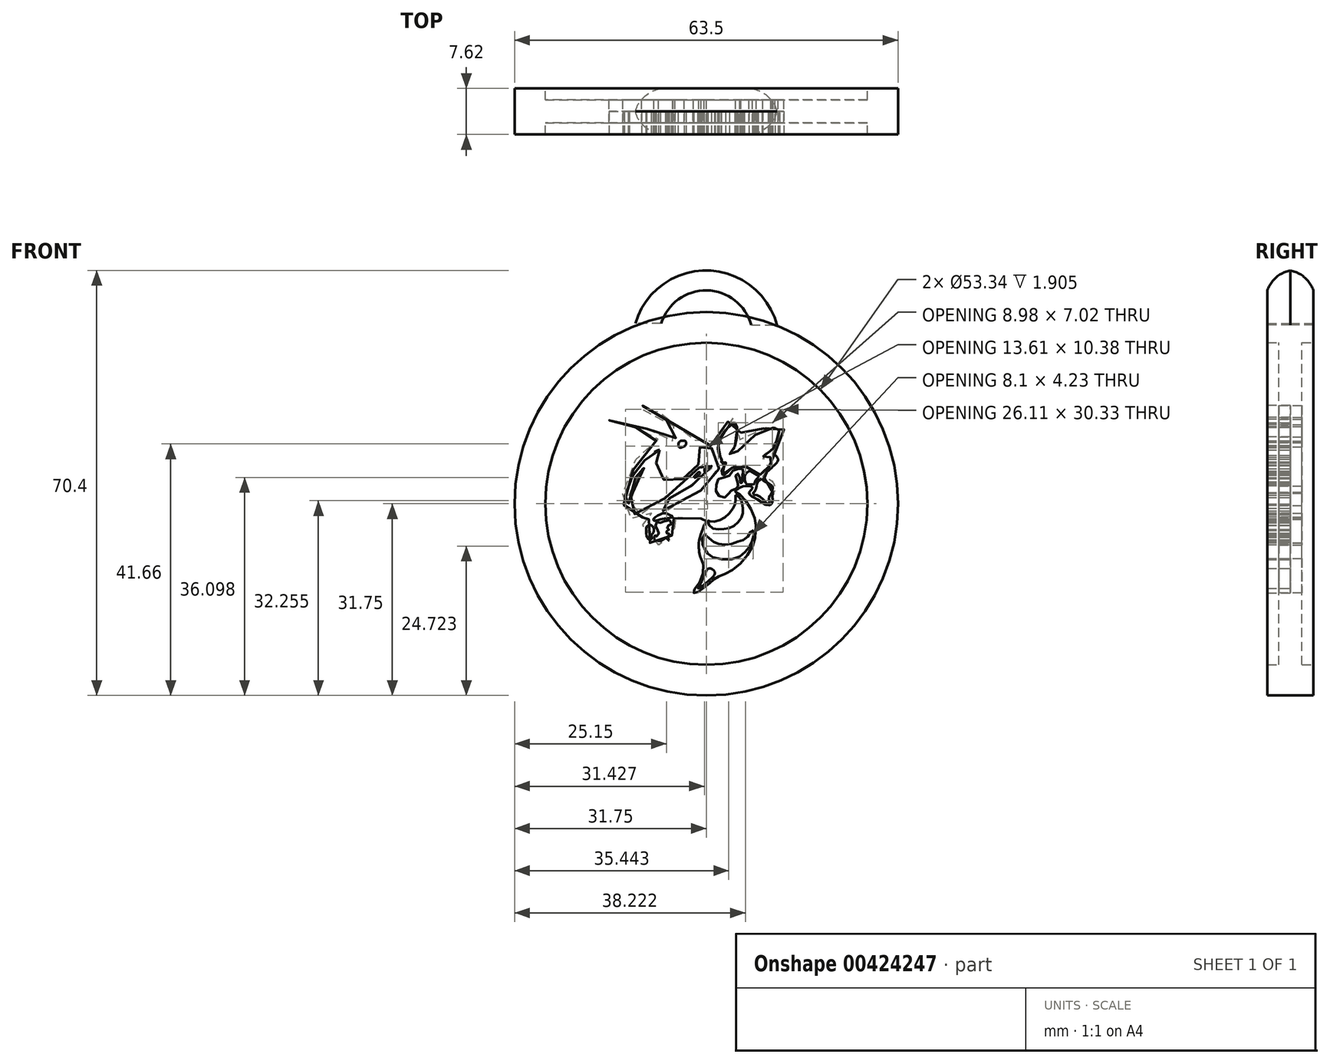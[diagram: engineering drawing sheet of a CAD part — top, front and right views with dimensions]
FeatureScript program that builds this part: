
annotation { "Feature Type Name" : "Feature", "Feature Type Description" : "" }
export const myFeature = defineFeature(function(context is Context, id is Id, definition is map)
    precondition{}
    {
        {
            var Q0;
            Q0=qCreatedBy(makeId("Front.planeOp"),FACE);
            var sketch = newSketch(context, id + "F0", { "sketchPlane" : qUnion([Q0])});
            skCircle(sketch, "E0", {"center": v(0, 0) * mm, "radius": 31.75 * mm});
            skCircle(sketch, "E1", {"center": v(0, 0) * mm, "radius": 26.67 * mm});
            skFitSpline(sketch, "E2", {"points": [v(0.48, -10.7) * mm, v(0.9, -10.8) * mm, v(1.39, -11.3) * mm, v(1.28, -11.82) * mm, v(0.74, -12.42) * mm, v(-1.36, -14.03) * mm, v(-0.8, -12.88) * mm, v(-0.23, -11.49) * mm, v(0.2, -10.85) * mm, v(0.48, -10.7) * mm]});
            skFitSpline(sketch, "E3", {"points": [v(-0.89, -9.06) * mm, v(-0.46, -10.42) * mm, v(-1.13, -13.06) * mm, v(-2.18, -14.47) * mm, v(-2.1, -14.76) * mm, v(-1.49, -14.63) * mm, v(-0.55, -13.96) * mm, v(0.85, -12.88) * mm, v(1.5, -12.34) * mm, v(2.52, -11.83) * mm, v(4.25, -10.99) * mm, v(6.68, -8.7) * mm, v(8, -6.02) * mm, v(8.17, -4.7) * mm, v(8.2, -3.57) * mm, v(7.74, -1.6) * mm, v(6.1, 1) * mm, v(5.22, 1.76) * mm, v(4.84, 1.94) * mm], "startDerivative": vector(10.59, -25.54) * mm, "endDerivative": vector(-11.94, 5.08) * mm});
            skFitSpline(sketch, "E4", {"points": [v(-0.89, -9.06) * mm, v(-1.1, -8.45) * mm, v(-1.23, -7.58) * mm, v(-1.27, -6.84) * mm, v(-1.1, -5.68) * mm, v(-0.37, -3.61) * mm, v(-0.12, -3.16) * mm, v(0, -2.93) * mm, v(-0.59, -2.6) * mm, v(-0.89, -2.46) * mm], "startDerivative": vector(-2.41, 5.48) * mm, "endDerivative": vector(-3.17, 1.59) * mm});
            skFitSpline(sketch, "E5", {"points": [v(0.22, -2.79) * mm, v(0.48, -2.81) * mm, v(0.7, -2.92) * mm, v(1.7, -2.87) * mm, v(2.89, -2.36) * mm, v(3.92, -1.48) * mm, v(4.69, -0.3) * mm, v(4.84, 0.53) * mm, v(4.83, 1.38) * mm, v(4.93, 1.4) * mm, v(5.3, 1.21) * mm, v(5.68, 0.77) * mm, v(5.9, 0.16) * mm, v(6.03, -0.77) * mm, v(6, -1.78) * mm, v(5.65, -2.58) * mm, v(4.8, -3.5) * mm, v(3.73, -4.02) * mm, v(2.66, -4.2) * mm, v(1.44, -4.2) * mm, v(0.54, -3.65) * mm, v(0.22, -2.79) * mm]});
            skFitSpline(sketch, "E6", {"points": [v(-0.3, -5.05) * mm, v(0.57, -5.81) * mm, v(1.43, -6.44) * mm, v(2.47, -6.75) * mm, v(3.88, -6.69) * mm, v(5.25, -6.26) * mm, v(6.26, -5.94) * mm, v(7.03, -5.18) * mm, v(7.4, -4.53) * mm, v(7.66, -4.41) * mm, v(7.91, -4.57) * mm, v(7.72, -5.7) * mm, v(7.12, -7.16) * mm, v(6.28, -8.1) * mm, v(4.84, -9.06) * mm, v(1.7, -9.06) * mm, v(0.27, -8.28) * mm, v(-0.33, -7.36) * mm, v(-0.6, -6.84) * mm, v(-0.67, -5.97) * mm, v(-0.3, -5.05) * mm]});
            skFitSpline(sketch, "E7", {"points": [v(-0.89, -2.46) * mm, v(-1.9, -2.24) * mm, v(-3.05, -2.22) * mm, v(-4.42, -2.24) * mm, v(-5.47, -2.46) * mm, v(-5.54, -3.32) * mm, v(-5.54, -3.84) * mm, v(-5.22, -4.32) * mm, v(-5.26, -4.7) * mm, v(-5.63, -4.9) * mm, v(-6, -6.44) * mm, v(-7.23, -6.44) * mm, v(-7.57, -6.75) * mm, v(-8.94, -6.66) * mm, v(-10.54, -5.26) * mm, v(-10.59, -3.78) * mm, v(-10.22, -3.1) * mm, v(-9.38, -2.5) * mm, v(-8.71, -1.9) * mm, v(-8.7, -1.6) * mm, v(-8.94, -1.54) * mm, v(-9.7, -1.79) * mm, v(-10.34, -2.2) * mm, v(-11.34, -2.5) * mm, v(-12.37, -2.5) * mm, v(-13.37, -1.11) * mm, v(-13.65, -0.25) * mm, v(-13.84, 0.97) * mm, v(-13.47, 2.99) * mm, v(-12.08, 5.7) * mm, v(-11.5, 7.95) * mm, v(-9.62, 10.14) * mm, v(-7.98, 10.52) * mm, v(-8.03, 10.81) * mm, v(-9.21, 11.62) * mm, v(-11.24, 12.48) * mm, v(-11.93, 12.77) * mm, v(-13.64, 12.8) * mm, v(-14.98, 13.02) * mm, v(-16.09, 13.73) * mm, v(-15.9, 13.91) * mm, v(-13.82, 13.85) * mm, v(-11.09, 12.97) * mm, v(-7.73, 11.34) * mm, v(-6.33, 10.49) * mm, v(-5.55, 10.43) * mm, v(-4.9, 11) * mm, v(-3.94, 11.07) * mm, v(-3.7, 11.25) * mm, v(-6.1, 13.43) * mm, v(-7.03, 14.16) * mm, v(-9.82, 15.25) * mm, v(-10.7, 15.76) * mm, v(-10.7, 16.02) * mm, v(-10.5, 16.25) * mm, v(-9.06, 15.8) * mm, v(-7.17, 14.78) * mm, v(-2.85, 11.28) * mm, v(-1.65, 10.49) * mm, v(0, 10.08) * mm, v(1.05, 9.43) * mm, v(1.8, 10.44) * mm, v(2.88, 12.74) * mm, v(3.7, 13.72) * mm, v(4.56, 14.3) * mm, v(5.33, 13.88) * mm, v(5.64, 12.74) * mm, v(5.74, 11.8) * mm, v(5.56, 10.13) * mm, v(6.76, 10.96) * mm, v(9.74, 12.57) * mm, v(10.5, 12.93) * mm, v(11.28, 13.11) * mm, v(12.12, 13.08) * mm, v(12.78, 12.63) * mm, v(12.59, 11.29) * mm, v(11.3, 9.2) * mm, v(10.7, 8.34) * mm, v(11.3, 8.11) * mm, v(11.7, 7.72) * mm, v(11.8, 7.04) * mm, v(9.35, 4.53) * mm, v(9.48, 4.32) * mm, v(10.07, 4.2) * mm, v(10.93, 3.7) * mm, v(11.27, 3.08) * mm, v(11.34, 2.25) * mm, v(11.03, 1.73) * mm], "startDerivative": vector(-94.1, 24.52) * mm, "endDerivative": vector(-56.35, -59.15) * mm});
            skFitSpline(sketch, "E8", {"points": [v(11.03, 1.73) * mm, v(10.93, 1.5) * mm, v(10.93, 1) * mm, v(11.03, 0.67) * mm, v(10.83, 0.1) * mm, v(10.6, -0.19) * mm, v(9.97, -0.2) * mm, v(8.24, 0.87) * mm, v(7.6, 1.18) * mm, v(7.13, 1.6) * mm, v(7.1, 1.92) * mm, v(7.52, 2.4) * mm, v(7.66, 2.68) * mm, v(7.36, 2.88) * mm, v(6.46, 2.97) * mm, v(5.8, 2.81) * mm, v(5.17, 2.42) * mm, v(4.84, 2.2) * mm, v(4.84, 1.94) * mm, v(4.96, 1.9) * mm], "startDerivative": vector(-3.16, -5.3) * mm, "endDerivative": vector(5.18, -0.7) * mm});
            skFitSpline(sketch, "E9", {"points": [v(9.17, 4.16) * mm, v(9.4, 3.93) * mm, v(10.1, 3.48) * mm, v(10.8, 3.07) * mm, v(10.98, 2.87) * mm, v(10.92, 2.14) * mm, v(10.7, 1.53) * mm, v(10.32, 1.05) * mm, v(10.53, 0.46) * mm, v(10.25, 0) * mm, v(9.92, 0.17) * mm, v(9.1, 0.98) * mm, v(8.4, 1.44) * mm, v(7.78, 1.55) * mm, v(7.78, 1.83) * mm, v(8.05, 2.1) * mm, v(8.2, 2.46) * mm, v(8.39, 3.2) * mm, v(8.4, 3.57) * mm, v(9.17, 4.16) * mm]});
            skFitSpline(sketch, "E10", {"points": [v(6.97, 5.35) * mm, v(7.39, 5.36) * mm, v(8.09, 4.96) * mm, v(8.64, 4.5) * mm, v(8.42, 4.14) * mm, v(8.1, 3.73) * mm, v(7.9, 3.25) * mm, v(7.25, 3.22) * mm, v(6.66, 3.24) * mm, v(6.36, 4.1) * mm, v(6.48, 4.84) * mm, v(6.97, 5.35) * mm]});
            skFitSpline(sketch, "E11", {"points": [v(6.01, 5.78) * mm, v(6.12, 5.49) * mm, v(6.12, 5.01) * mm, v(6, 4.8) * mm, v(5.98, 3.92) * mm, v(5.8, 3.83) * mm, v(6, 3.64) * mm, v(5.8, 3.4) * mm, v(5.58, 3.67) * mm, v(5.44, 4.9) * mm, v(5.1, 4.96) * mm, v(4.86, 4.7) * mm, v(5.2, 3.5) * mm, v(5.28, 2.98) * mm, v(5.1, 2.7) * mm, v(4.48, 2.3) * mm, v(3.83, 1.95) * mm, v(3.4, 1.2) * mm, v(2.33, 1.15) * mm, v(1.6, 2.05) * mm, v(1.69, 3.34) * mm, v(2.26, 4.28) * mm, v(3.55, 4.47) * mm, v(4.36, 5.47) * mm, v(5.1, 5.76) * mm, v(6.01, 5.78) * mm]});
            skFitSpline(sketch, "E12", {"points": [v(4.55, 13.42) * mm, v(4.22, 13.39) * mm, v(3.42, 12.48) * mm, v(2.78, 11.56) * mm, v(2.2, 10.58) * mm, v(1.96, 9.66) * mm, v(2.08, 8.23) * mm, v(2.54, 7.31) * mm, v(2.5, 6.85) * mm, v(3.06, 6.88) * mm, v(3.27, 6.73) * mm, v(2.66, 5.85) * mm, v(2.54, 5.2) * mm, v(2.81, 4.75) * mm, v(4.36, 6.06) * mm, v(6.66, 6.1) * mm, v(8.95, 4.8) * mm, v(10.78, 6.6) * mm, v(10.81, 7.59) * mm, v(10.63, 7.74) * mm, v(9.32, 7.4) * mm, v(10.36, 8.87) * mm, v(11.06, 9.12) * mm, v(10.96, 9.4) * mm, v(12.06, 11.03) * mm, v(12.14, 12.12) * mm, v(11.8, 12.63) * mm, v(11.28, 12.63) * mm, v(7.89, 11.22) * mm, v(4.36, 8.07) * mm, v(3.89, 8.13) * mm, v(4, 8.55) * mm, v(4.56, 9.2) * mm, v(5.1, 11.99) * mm, v(4.93, 13.11) * mm, v(4.55, 13.42) * mm]});
            skFitSpline(sketch, "E13", {"points": [v(-3.98, 10.47) * mm, v(-3.39, 10.29) * mm, v(-3.39, 9.78) * mm, v(-3.86, 9.42) * mm, v(-4.47, 9.35) * mm, v(-4.57, 10.1) * mm, v(-3.98, 10.47) * mm]});
            skFitSpline(sketch, "E14", {"points": [v(-7.72, 8.92) * mm, v(-8.57, 8.59) * mm, v(-10.11, 7.33) * mm, v(-11.37, 5.9) * mm, v(-12.33, 4.38) * mm, v(-13.19, 2.34) * mm, v(-13.47, 0.57) * mm, v(-12.94, -0.71) * mm, v(-12.86, 0.8) * mm, v(-12.08, 3.77) * mm, v(-9.83, 6.75) * mm, v(-11.78, 3.37) * mm, v(-12.56, 0.62) * mm, v(-12.56, -1.04) * mm, v(-11.17, -1.8) * mm, v(-4.92, 2.61) * mm, v(0, 6.87) * mm, v(0.53, 6.9) * mm, v(0.85, 6.32) * mm, v(0.68, 5.49) * mm, v(-3.8, 2.14) * mm, v(-5.5, 1.28) * mm, v(-8.27, -0.89) * mm, v(-4.9, -0.49) * mm, v(1.26, 4.35) * mm, v(2.14, 6) * mm, v(1.72, 8.35) * mm, v(0.24, 9.53) * mm, v(-0.75, 9.7) * mm, v(-1.02, 9.6) * mm, v(-0.95, 8.7) * mm, v(-1.13, 7.15) * mm, v(-1.65, 6) * mm, v(-3.39, 4.42) * mm, v(-5.24, 3.69) * mm, v(-6.75, 3.83) * mm, v(-7.9, 4.83) * mm, v(-8.33, 6.5) * mm, v(-7.97, 8.14) * mm, v(-7.56, 8.75) * mm, v(-7.72, 8.92) * mm]});
            skFitSpline(sketch, "E15", {"points": [v(-1.16, 5.24) * mm, v(-2.02, 4.38) * mm, v(-1.11, 4.88) * mm, v(-1.16, 5.24) * mm]});
            skFitSpline(sketch, "E16", {"points": [v(-0.26, 5.86) * mm, v(-0.28, 5.32) * mm, v(0.21, 5.6) * mm, v(0.26, 6.17) * mm, v(0, 6.3) * mm, v(-0.26, 5.86) * mm]});
            skFitSpline(sketch, "E17", {"points": [v(-7.24, -1.58) * mm, v(-6.42, -1.67) * mm, v(-5.59, -2.17) * mm, v(-6.1, -2.34) * mm, v(-7.12, -2.46) * mm, v(-8.3, -2.78) * mm, v(-8.7, -2.75) * mm, v(-8.73, -2.46) * mm, v(-7.24, -1.58) * mm]});
            skFitSpline(sketch, "E18", {"points": [v(-8.2, -3.02) * mm, v(-7.65, -3.12) * mm, v(-6.96, -2.86) * mm, v(-5.9, -2.8) * mm, v(-5.9, -3.5) * mm, v(-6.45, -3.6) * mm, v(-6.45, -4.02) * mm, v(-6.2, -4.21) * mm, v(-6.41, -4.53) * mm, v(-6.65, -4.6) * mm, v(-6.63, -4.86) * mm, v(-6.12, -4.9) * mm, v(-6.33, -5.34) * mm, v(-6.2, -5.9) * mm, v(-6.27, -6.09) * mm, v(-6.74, -5.56) * mm, v(-7, -5.8) * mm, v(-7.8, -6.19) * mm, v(-8.49, -6.05) * mm, v(-8.63, -5.87) * mm, v(-8.64, -5.45) * mm, v(-8.41, -5.21) * mm, v(-8.26, -5.4) * mm, v(-7.93, -5.14) * mm, v(-8.06, -4.26) * mm, v(-8.45, -3.72) * mm, v(-8.2, -3.02) * mm]});
            skFitSpline(sketch, "E19", {"points": [v(-9.42, -3.5) * mm, v(-9.02, -3.63) * mm, v(-8.7, -4) * mm, v(-8.76, -4.73) * mm, v(-9.08, -5.18) * mm, v(-9.1, -5.85) * mm, v(-9.5, -5.93) * mm, v(-9.8, -5.55) * mm, v(-9.9, -3.9) * mm, v(-9.42, -3.5) * mm]});
            skSolve(sketch);
        }
        {
            var Q0;
            Q0=makeQuery(id+"F0.imprint","IMPRINT",FACE,{"disambiguationData":[TD([[makeQuery(id+"F0.imprint","IMPRINT",EDGE,{"derivedFrom":sQuery(id+"F0.wireOp",EDGE,"E0")}),1.0]])]});
            extrude(context, id + "F1", {"entities" : qUnion([Q0]), "endBound" : BoundingType.SYMMETRIC, "depth" : 7.62 * mm});
        }
        {
            var Q0;
            Q0=makeQuery(id+"F0.imprint","IMPRINT",FACE,{"disambiguationData":[TD([[makeQuery(id+"F0.imprint","IMPRINT",EDGE,{"derivedFrom":sQuery(id+"F0.wireOp",EDGE,"E1")}),1.0]])]});
            extrude(context, id + "F2", {"entities" : qUnion([Q0]), "operationType" : NewBodyOperationType.ADD, "endBound" : BoundingType.SYMMETRIC, "depth" : 3.8 * mm});
        }
        {
            var Q0;
            Q0=makeQuery(id+"F0.imprint","IMPRINT",FACE,{"disambiguationData":[TD([[makeQuery(id+"F0.imprint","IMPRINT",EDGE,{"derivedFrom":sQuery(id+"F0.wireOp",EDGE,"E14")}),1.0]])]});
            var Q1;
            Q1=makeQuery(id+"F0.imprint","IMPRINT",FACE,{"disambiguationData":[TD([[makeQuery(id+"F0.imprint","IMPRINT",EDGE,{"derivedFrom":sQuery(id+"F0.wireOp",EDGE,"E5")}),-1.0]])]});
            var Q2;
            Q2=makeQuery(id+"F0.imprint","IMPRINT",FACE,{"disambiguationData":[TD([[makeQuery(id+"F0.imprint","IMPRINT",EDGE,{"derivedFrom":sQuery(id+"F0.wireOp",EDGE,"E6")}),-1.0]])]});
            var Q3;
            Q3=makeQuery(id+"F0.imprint","IMPRINT",FACE,{"disambiguationData":[TD([[makeQuery(id+"F0.imprint","IMPRINT",EDGE,{"derivedFrom":sQuery(id+"F0.wireOp",EDGE,"E11")}),-1.0]])]});
            var Q4;
            Q4=makeQuery(id+"F0.imprint","IMPRINT",FACE,{"disambiguationData":[TD([[makeQuery(id+"F0.imprint","IMPRINT",EDGE,{"derivedFrom":sQuery(id+"F0.wireOp",EDGE,"E12")}),1.0]])]});
            var Q5;
            Q5=makeQuery(id+"F0.imprint","IMPRINT",FACE,{"disambiguationData":[TD([[makeQuery(id+"F0.imprint","IMPRINT",EDGE,{"derivedFrom":sQuery(id+"F0.wireOp",EDGE,"E9")}),-1.0]])]});
            var Q6;
            Q6=makeQuery(id+"F0.imprint","IMPRINT",FACE,{"disambiguationData":[TD([[makeQuery(id+"F0.imprint","IMPRINT",EDGE,{"derivedFrom":sQuery(id+"F0.wireOp",EDGE,"E10")}),-1.0]])]});
            var Q7;
            Q7=makeQuery(id+"F0.imprint","IMPRINT",FACE,{"disambiguationData":[TD([[makeQuery(id+"F0.imprint","IMPRINT",EDGE,{"derivedFrom":sQuery(id+"F0.wireOp",EDGE,"E2")}),-1.0]])]});
            var Q8;
            Q8=makeQuery(id+"F0.imprint","IMPRINT",FACE,{"disambiguationData":[TD([[makeQuery(id+"F0.imprint","IMPRINT",EDGE,{"derivedFrom":sQuery(id+"F0.wireOp",EDGE,"E18")}),-1.0]])]});
            var Q9;
            Q9=makeQuery(id+"F0.imprint","IMPRINT",FACE,{"disambiguationData":[TD([[makeQuery(id+"F0.imprint","IMPRINT",EDGE,{"derivedFrom":sQuery(id+"F0.wireOp",EDGE,"E17")}),-1.0]])]});
            var Q10;
            Q10=makeQuery(id+"F0.imprint","IMPRINT",FACE,{"disambiguationData":[TD([[makeQuery(id+"F0.imprint","IMPRINT",EDGE,{"derivedFrom":sQuery(id+"F0.wireOp",EDGE,"E13")}),-1.0]])]});
            var Q11;
            Q11=makeQuery(id+"F0.imprint","IMPRINT",FACE,{"disambiguationData":[TD([[makeQuery(id+"F0.imprint","IMPRINT",EDGE,{"derivedFrom":sQuery(id+"F0.wireOp",EDGE,"E15")}),1.0]])]});
            var Q12;
            Q12=makeQuery(id+"F0.imprint","IMPRINT",FACE,{"disambiguationData":[TD([[makeQuery(id+"F0.imprint","IMPRINT",EDGE,{"derivedFrom":sQuery(id+"F0.wireOp",EDGE,"E16")}),1.0]])]});
            var Q13;
            Q13=makeQuery(id+"F0.imprint","IMPRINT",FACE,{"disambiguationData":[TD([[makeQuery(id+"F0.imprint","IMPRINT",EDGE,{"derivedFrom":sQuery(id+"F0.wireOp",EDGE,"E19")}),-1.0]])]});
            extrude(context, id + "F3", {"entities" : qUnion([Q0, Q1, Q2, Q3, Q4, Q5, Q6, Q7, Q8, Q9, Q10, Q11, Q12, Q13]), "depth" : 1.9 * mm});
        }
        {
            var Q0;
            Q0=makeQuery(id+"F0.imprint","IMPRINT",FACE,{"disambiguationData":[TD([[makeQuery(id+"F0.imprint","IMPRINT",EDGE,{"derivedFrom":sQuery(id+"F0.wireOp",EDGE,"E2")}),1.0]])]});
            extrude(context, id + "F4", {"entities" : qUnion([Q0]), "depth" : 3.8 * mm});
        }
        {
            var Q0;
            Q0=qCreatedBy(makeId("Front.planeOp"),FACE);
            var sketch = newSketch(context, id + "F5", { "sketchPlane" : qUnion([Q0])});
            skArc(sketch, "E20", {"start": v(7.43, 29.6) * mm, "mid": v(0.08, 35.34) * mm, "end": v(-7.47, 29.85) * mm});
            skLineSegment(sketch, "E21", {"start": v(7.43, 29.6) * mm, "end": v(11.88, 29.6) * mm});
            skLineSegment(sketch, "E22", {"start": v(-7.47, 29.85) * mm, "end": v(-11.92, 29.85) * mm});
            skArc(sketch, "E23", {"start": v(11.88, 29.6) * mm, "mid": v(0.08, 38.74) * mm, "end": v(-11.92, 29.85) * mm});
            skSolve(sketch);
        }
        {
            var Q0;
            Q0=makeQuery(id+"F5.imprint","IMPRINT",FACE,{"disambiguationData":[TD([[makeQuery(id+"F5.imprint","IMPRINT",EDGE,{"derivedFrom":sQuery(id+"F5.wireOp",EDGE,"E20")}),-1.0]])]});
            extrude(context, id + "F6", {"entities" : qUnion([Q0]), "endBound" : BoundingType.SYMMETRIC, "depth" : 7.62 * mm});
        }
        {
            var Q0;
            Q0=makeQuery(id+"F6.opExtrude","CAP_EDGE",EDGE,{"disambiguationData":[OSD([sQuery(id+"F5.wireOp",EDGE,"E23")])],"isStart":true});
            var Q1;
            Q1=makeQuery(id+"F6.opExtrude","CAP_EDGE",EDGE,{"disambiguationData":[OSD([sQuery(id+"F5.wireOp",EDGE,"E23")])],"isStart":false});
            fillet(context, id + "F7", {"entities" : qUnion([Q0, Q1]), "radius" : 5.08 * mm, "tangentPropagation" : true, "allowEdgeOverflow" : false});
        }
    });
